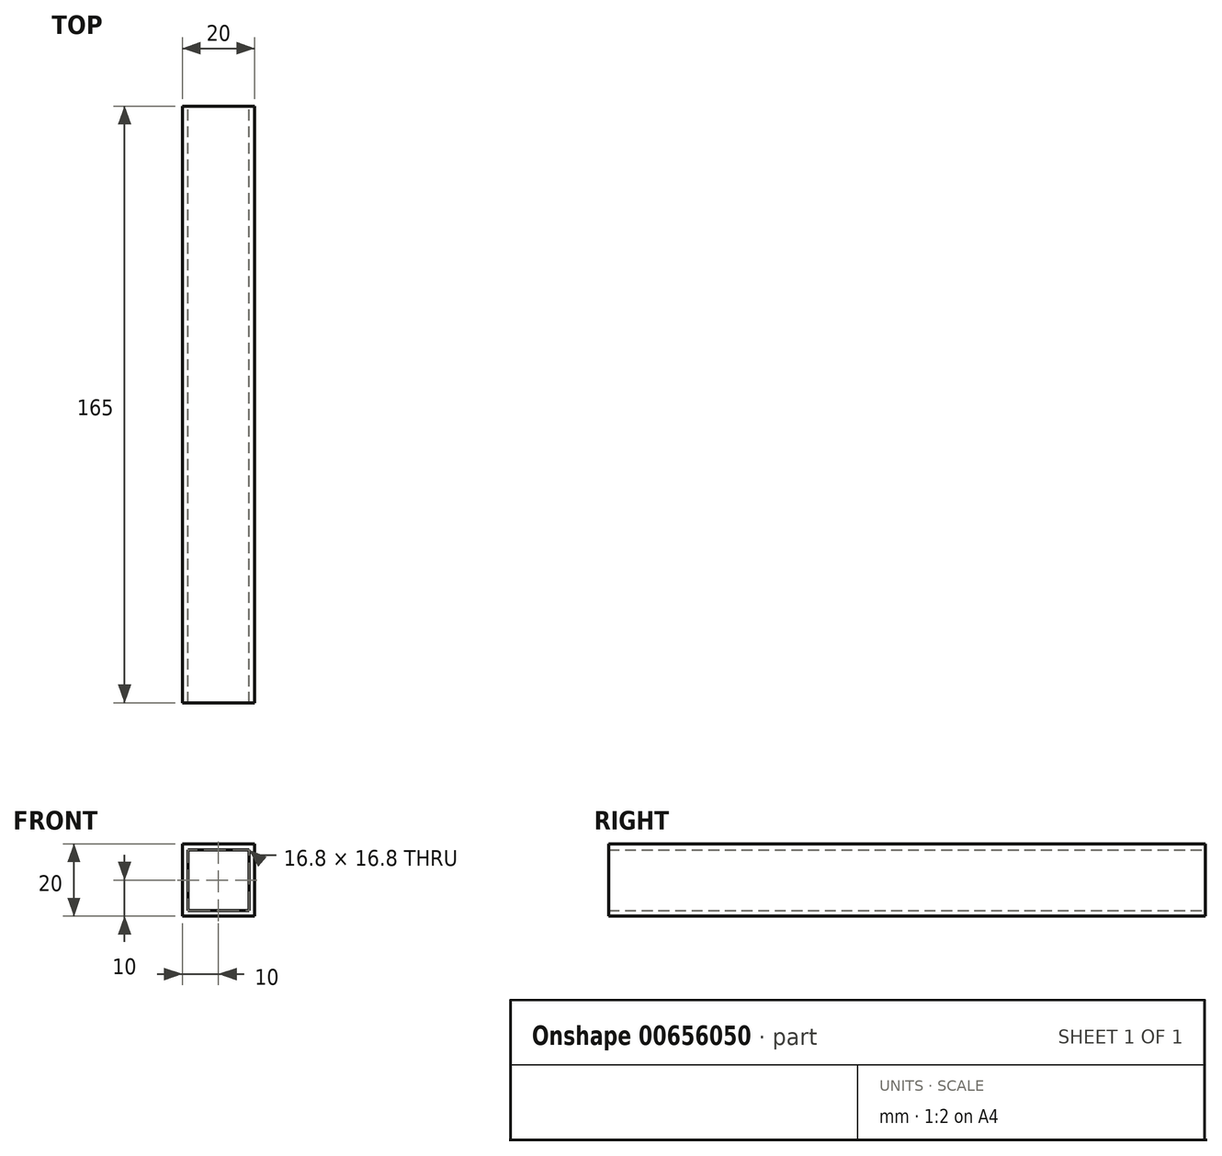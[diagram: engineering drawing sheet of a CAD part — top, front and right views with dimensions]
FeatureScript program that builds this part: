
annotation { "Feature Type Name" : "Feature", "Feature Type Description" : "" }
export const myFeature = defineFeature(function(context is Context, id is Id, definition is map)
    precondition{}
    {
        {
            var Q0;
            Q0=qCreatedBy(makeId("Front.planeOp"),FACE);
            var sketch = newSketch(context, id + "F0", { "sketchPlane" : qUnion([Q0])});
            skLineSegment(sketch, "E0.bottom", {"start": v(0, 0) * mm, "end": v(20, 0) * mm});
            skLineSegment(sketch, "E0.top", {"start": v(0, -20) * mm, "end": v(20, -20) * mm});
            skLineSegment(sketch, "E0.left", {"start": v(0, 0) * mm, "end": v(0, -20) * mm});
            skLineSegment(sketch, "E0.right", {"start": v(20, 0) * mm, "end": v(20, -20) * mm});
            skLineSegment(sketch, "E1.0", {"start": v(1.6, -1.6) * mm, "end": v(18.4, -1.6) * mm});
            skLineSegment(sketch, "E1.1", {"start": v(1.6, -1.6) * mm, "end": v(1.6, -18.4) * mm});
            skLineSegment(sketch, "E1.2", {"start": v(1.6, -18.4) * mm, "end": v(18.4, -18.4) * mm});
            skLineSegment(sketch, "E1.3", {"start": v(18.4, -1.6) * mm, "end": v(18.4, -18.4) * mm});
            skSolve(sketch);
        }
        {
            var Q0;
            Q0=makeQuery(id+"F0.imprint","IMPRINT",FACE,{"disambiguationData":[TD([[makeQuery(id+"F0.imprint","IMPRINT",EDGE,{"derivedFrom":sQuery(id+"F0.wireOp",EDGE,"E0.bottom")}),-1.0]])]});
            extrude(context, id + "F1", {"entities" : qUnion([Q0]), "depth" : 167 * mm - 2 * mm, "offsetDistance" : 25.4 * mm});
        }
    });
